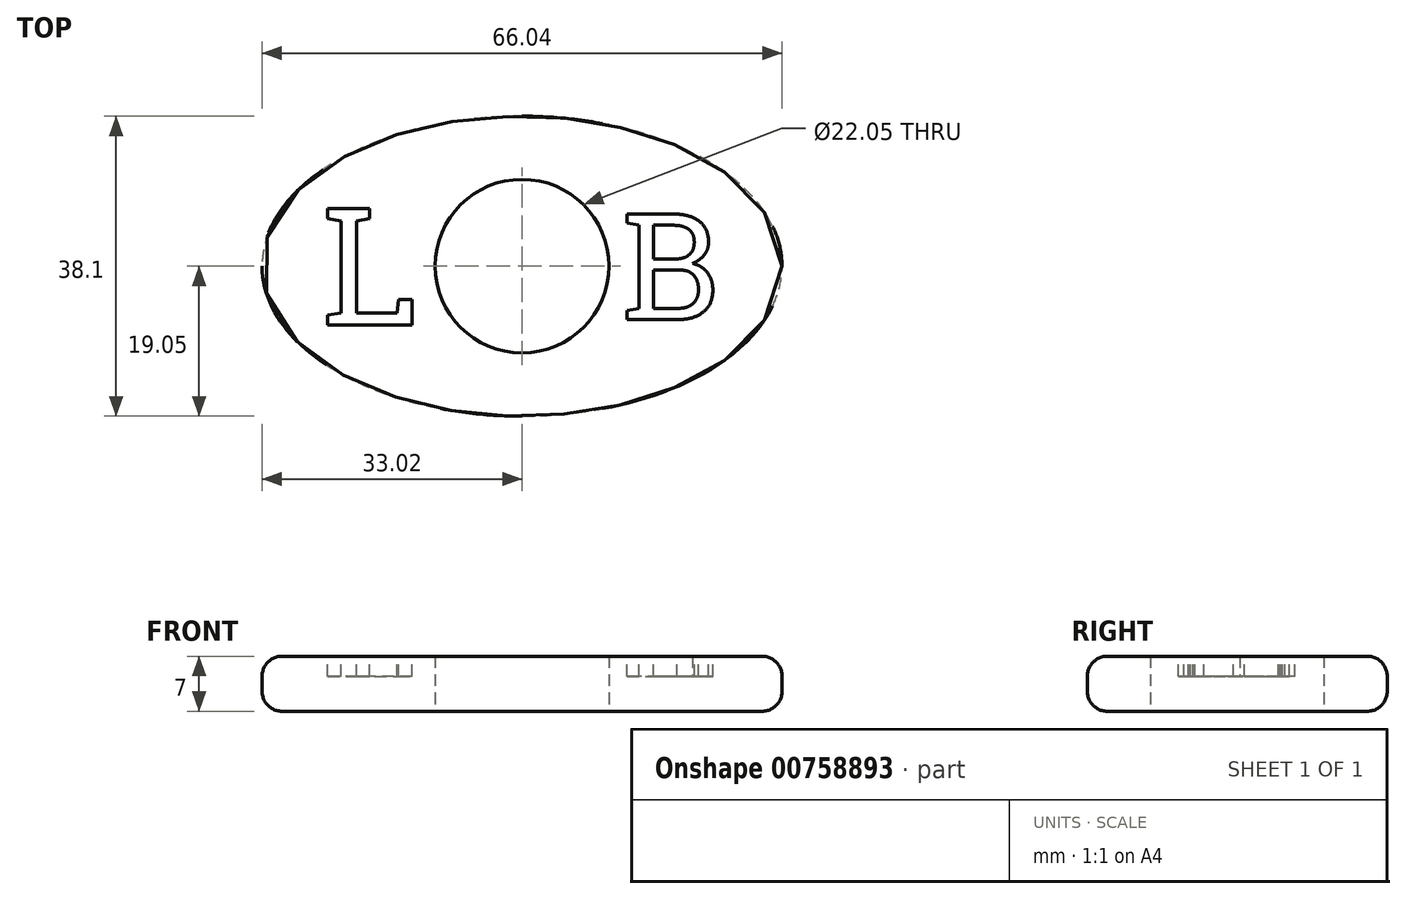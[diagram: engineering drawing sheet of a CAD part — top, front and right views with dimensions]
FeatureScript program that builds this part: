
annotation { "Feature Type Name" : "Feature", "Feature Type Description" : "" }
export const myFeature = defineFeature(function(context is Context, id is Id, definition is map)
    precondition{}
    {
        {
            var Q0;
            Q0=qCreatedBy(makeId("Top.planeOp"),FACE);
            var sketch = newSketch(context, id + "F0", { "sketchPlane" : qUnion([Q0])});
            skEllipse(sketch, "E0", {"center": v(0, 0) * mm, "majorRadius": 33.02 * mm, "minorRadius": 19.05 * mm, "majorAxis": v(1, 0)});
            skCircle(sketch, "E1", {"center": v(0, 0) * mm, "radius": 11.03 * mm});
            skLineSegment(sketch, "E2", {"start": v(-33.02, 0) * mm, "end": v(33.02, 0) * mm, "construction": true});
            skLineSegment(sketch, "E3", {"start": v(0, 19.05) * mm, "end": v(0, -19.05) * mm, "construction": true});
            skSolve(sketch);
        }
        {
            var Q0;
            Q0=makeQuery(id+"F0.imprint","IMPRINT",FACE,{"disambiguationData":[TD([[makeQuery(id+"F0.imprint","IMPRINT",EDGE,{"derivedFrom":sQuery(id+"F0.wireOp",EDGE,"E0")}),1.0]])]});
            extrude(context, id + "F1", {"entities" : qUnion([Q0]), "depth" : 7 * mm, "offsetDistance" : 25.4 * mm});
        }
        {
            var Q0;
            Q0=makeQuery(id+"F1.opExtrude","CAP_EDGE",EDGE,{"disambiguationData":[OSD([sQuery(id+"F0.wireOp",EDGE,"E0")])],"isStart":false});
            var Q1;
            Q1=makeQuery(id+"F1.opExtrude","CAP_EDGE",EDGE,{"disambiguationData":[OSD([sQuery(id+"F0.wireOp",EDGE,"E0")])],"isStart":true});
            fillet(context, id + "F2", {"entities" : qUnion([Q0, Q1]), "radius" : 2.54 * mm, "tangentPropagation" : true, "allowEdgeOverflow" : false});
        }
        {
            var Q0;
            Q0=makeQuery(id+"F1.opExtrude","CAP_FACE",FACE,{"disambiguationData":[OSD([sQuery(id+"F0.wireOp",EDGE,"E0"),sQuery(id+"F0.wireOp",EDGE,"E1")])],"isStart":false});
            var sketch = newSketch(context, id + "F3", { "sketchPlane" : qUnion([Q0])});
            skSolve(sketch);
        }
        {
            var Q0;
            {var subQ0=sQuery(id+"F0.wireOp",EDGE,"E1");Q0=makeQuery(id+"F3.imprint","IMPRINT",FACE,{"disambiguationData":[TD([[makeQuery(id+"F3.imprint","IMPRINT",EDGE,{"derivedFrom":makeQuery(id+"F1.opExtrude","CAP_EDGE",EDGE,{"disambiguationData":[OSD([subQ0])],"isStart":false})}),-1.0]])]});}
            var sketch = newSketch(context, id + "F4", { "sketchPlane" : qUnion([Q0])});
            skText(sketch, "E4", { "text": "L", "fontName": "RobotoSlab-Regular.ttf"});
            skText(sketch, "E5", { "text": "B", "fontName": "RobotoSlab-Regular.ttf"});
            skLineSegment(sketch, "E6", {"start": v(0, 0) * mm, "end": v(-25.4, 0) * mm, "construction": true});
            skLineSegment(sketch, "E7", {"start": v(0, 0) * mm, "end": v(25.4, 0) * mm, "construction": true});
            skLineSegment(sketch, "E8", {"start": v(-25.4, 0) * mm, "end": v(-12.7, 0) * mm, "construction": true});
            skLineSegment(sketch, "E9", {"start": v(12.7, 0) * mm, "end": v(25.4, 0) * mm});
            skPoint(sketch, "E10", {"position": v(19.05, 0) * mm});
            skLineSegment(sketch, "E11", {"start": v(12.7, 0) * mm, "end": v(25.4, 0) * mm, "construction": true});
            skPoint(sketch, "E12", {"position": v(-19.05, 0) * mm});
            const initialGuessF4  = {"E4": [-0.0254, -0.0075, 1, 0, 0.01502], "E5": [0.0127, -0.00678, 1, 0, 0.01357]};
            skSetInitialGuess(sketch, initialGuessF4);
            skSolve(sketch);
        }
        {
            var Q0;
            Q0=qSketchRegion(id+"F4",true);
            extrude(context, id + "F5", {"entities" : qUnion([Q0]), "operationType" : NewBodyOperationType.REMOVE, "oppositeDirection" : true, "depth" : 2.54 * mm, "offsetDistance" : 25.4 * mm});
        }
    });
